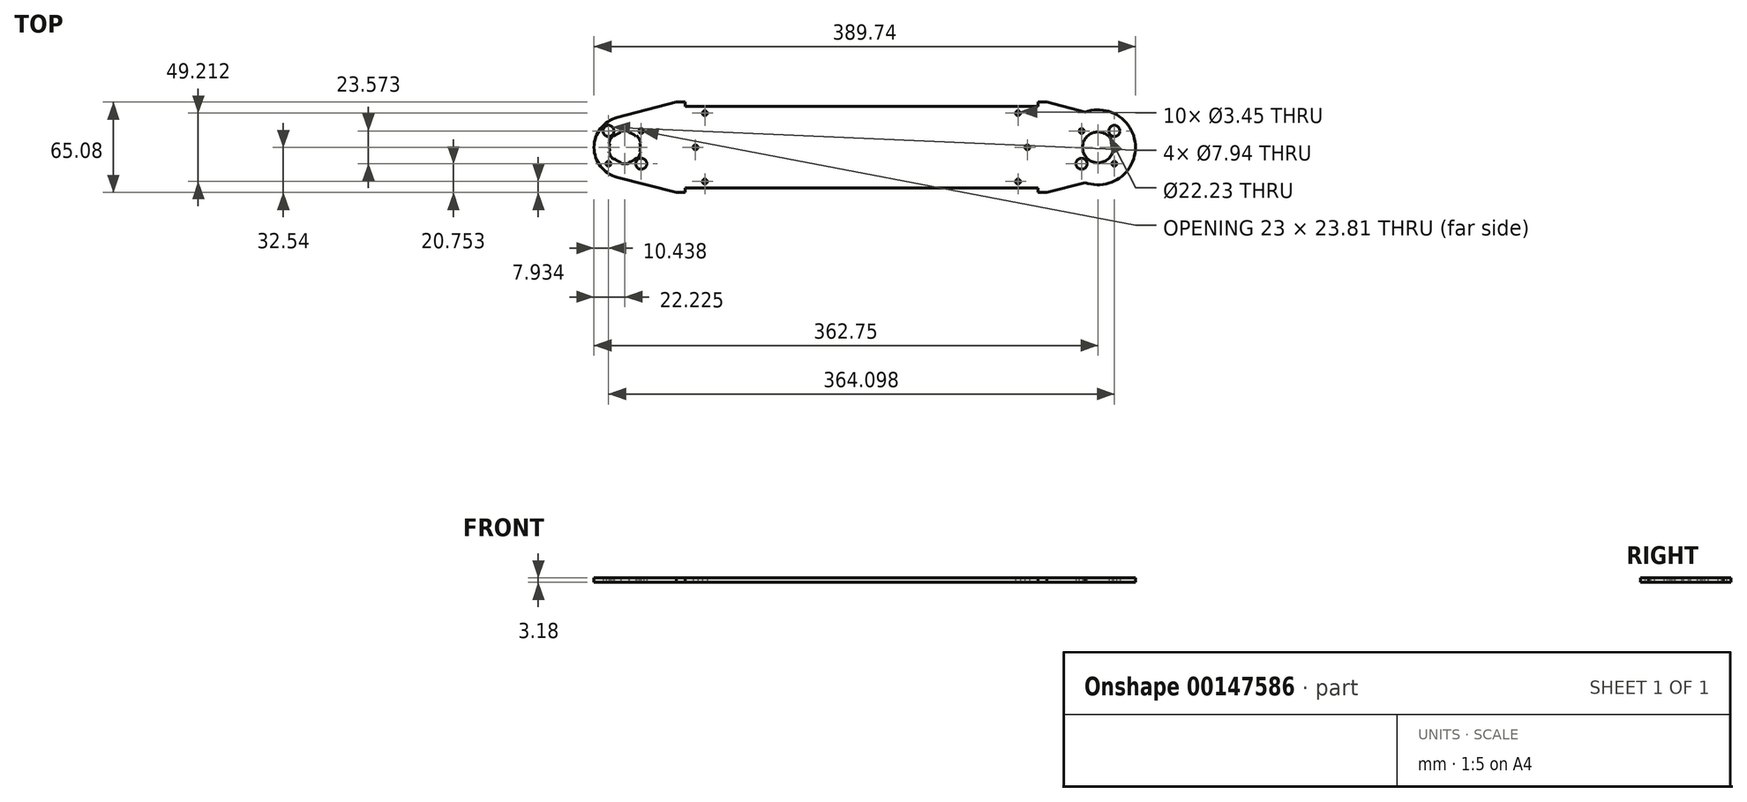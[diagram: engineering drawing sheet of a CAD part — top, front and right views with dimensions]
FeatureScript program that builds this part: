
annotation { "Feature Type Name" : "Feature", "Feature Type Description" : "" }
export const myFeature = defineFeature(function(context is Context, id is Id, definition is map)
    precondition{}
    {
        {
            var Q0;
            Q0=qCreatedBy(makeId("Top.planeOp"),FACE);
            var sketch = newSketch(context, id + "F0", { "sketchPlane" : qUnion([Q0])});
            skPoint(sketch, "E0.rect.middle", {"position": v(0, 0) * mm});
            skCircle(sketch, "E1", {"center": v(0, 0) * mm, "radius": 11.11 * mm});
            skLineSegment(sketch, "E2.bottom", {"start": v(11.79, 11.79) * mm, "end": v(-11.79, 11.79) * mm, "construction": true});
            skLineSegment(sketch, "E2.left", {"start": v(11.79, 11.79) * mm, "end": v(11.79, -11.79) * mm, "construction": true});
            skLineSegment(sketch, "E2.right", {"start": v(-11.79, 11.79) * mm, "end": v(-11.79, -11.79) * mm, "construction": true});
            skCircle(sketch, "E3", {"center": v(-11.79, 11.79) * mm, "radius": 1.73 * mm});
            skCircle(sketch, "E4", {"center": v(11.79, 11.79) * mm, "radius": 3.97 * mm});
            skCircle(sketch, "E5", {"center": v(11.79, -11.79) * mm, "radius": 1.73 * mm});
            skCircle(sketch, "E6", {"center": v(-11.79, -11.79) * mm, "radius": 3.97 * mm});
            skArc(sketch, "E7", {"start": v(-346.1, 21.51) * mm, "mid": v(-362.75, 0) * mm, "end": v(-346.1, -21.51) * mm});
            skLineSegment(sketch, "E8.bottom", {"start": v(-352.31, 11.79) * mm, "end": v(-328.74, 11.79) * mm, "construction": true});
            skLineSegment(sketch, "E8.top", {"start": v(-352.31, -11.79) * mm, "end": v(-328.74, -11.79) * mm, "construction": true});
            skLineSegment(sketch, "E8.left", {"start": v(-352.31, 11.79) * mm, "end": v(-352.31, -11.79) * mm, "construction": true});
            skLineSegment(sketch, "E8.right", {"start": v(-328.74, 11.79) * mm, "end": v(-328.74, -11.79) * mm, "construction": true});
            skCircle(sketch, "E9", {"center": v(-328.74, 11.79) * mm, "radius": 1.73 * mm});
            skCircle(sketch, "E10", {"center": v(-340.53, 0) * mm, "radius": 11.11 * mm});
            skCircle(sketch, "E11", {"center": v(-352.31, 11.79) * mm, "radius": 3.97 * mm});
            skCircle(sketch, "E12", {"center": v(-352.31, -11.79) * mm, "radius": 1.73 * mm});
            skCircle(sketch, "E13", {"center": v(-328.74, -11.79) * mm, "radius": 3.97 * mm});
            skLineSegment(sketch, "E14", {"start": v(0, 0) * mm, "end": v(-340.53, 0) * mm, "construction": true});
            skLineSegment(sketch, "E15", {"start": v(-346.1, -21.51) * mm, "end": v(-303.61, -32.54) * mm});
            skLineSegment(sketch, "E16", {"start": v(-346.1, 21.51) * mm, "end": v(-303.61, 32.54) * mm});
            skLineSegment(sketch, "E17", {"start": v(-297.26, -29.37) * mm, "end": v(-43.26, -29.37) * mm});
            skLineSegment(sketch, "E18", {"start": v(-297.26, 29.37) * mm, "end": v(-43.26, 29.37) * mm});
            skLineSegment(sketch, "E19", {"start": v(-297.26, 32.54) * mm, "end": v(-297.26, 29.37) * mm});
            skLineSegment(sketch, "E20", {"start": v(-297.26, 32.54) * mm, "end": v(-303.61, 32.54) * mm});
            skLineSegment(sketch, "E21", {"start": v(-297.26, -29.37) * mm, "end": v(-297.26, -32.54) * mm});
            skLineSegment(sketch, "E22", {"start": v(-297.26, -32.54) * mm, "end": v(-303.61, -32.54) * mm});
            skLineSegment(sketch, "E23", {"start": v(-43.26, -29.37) * mm, "end": v(-43.26, -32.54) * mm});
            skLineSegment(sketch, "E24", {"start": v(-43.26, -32.54) * mm, "end": v(-36.91, -32.54) * mm});
            skLineSegment(sketch, "E25", {"start": v(-43.26, 29.37) * mm, "end": v(-43.26, 32.54) * mm});
            skLineSegment(sketch, "E26", {"start": v(-43.26, 32.54) * mm, "end": v(-36.91, 32.54) * mm});
            skLineSegment(sketch, "E27", {"start": v(-36.91, -32.54) * mm, "end": v(-9.23, -25.36) * mm});
            skLineSegment(sketch, "E28", {"start": v(-9.23, 25.36) * mm, "end": v(-36.91, 32.54) * mm});
            skLineSegment(sketch, "E29", {"start": v(-297.26, 29.37) * mm, "end": v(-297.26, 24.6) * mm, "construction": true});
            skLineSegment(sketch, "E30", {"start": v(-297.26, 24.6) * mm, "end": v(-282.98, 24.6) * mm, "construction": true});
            skLineSegment(sketch, "E31", {"start": v(-297.26, -29.37) * mm, "end": v(-297.26, -24.6) * mm, "construction": true});
            skLineSegment(sketch, "E32", {"start": v(-297.26, -24.6) * mm, "end": v(-282.98, -24.6) * mm, "construction": true});
            skLineSegment(sketch, "E33", {"start": v(-43.26, -29.37) * mm, "end": v(-43.26, -24.6) * mm, "construction": true});
            skLineSegment(sketch, "E34", {"start": v(-43.26, -24.6) * mm, "end": v(-57.55, -24.6) * mm, "construction": true});
            skLineSegment(sketch, "E35", {"start": v(-43.26, 29.37) * mm, "end": v(-43.26, 24.6) * mm, "construction": true});
            skLineSegment(sketch, "E36", {"start": v(-43.26, 24.6) * mm, "end": v(-57.55, 24.6) * mm, "construction": true});
            skCircle(sketch, "E37", {"center": v(-282.98, 24.6) * mm, "radius": 1.73 * mm});
            skCircle(sketch, "E38", {"center": v(-57.55, 24.6) * mm, "radius": 1.73 * mm});
            skCircle(sketch, "E39", {"center": v(-57.55, -24.6) * mm, "radius": 1.73 * mm});
            skCircle(sketch, "E40", {"center": v(-282.98, -24.6) * mm, "radius": 1.73 * mm});
            skLineSegment(sketch, "E41", {"start": v(-11.79, -11.79) * mm, "end": v(11.79, -11.79) * mm, "construction": true});
            skLineSegment(sketch, "E42", {"start": v(-170.26, -29.37) * mm, "end": v(-170.26, 0) * mm, "construction": true});
            skLineSegment(sketch, "E43", {"start": v(-170.26, 0) * mm, "end": v(-170.26, 29.37) * mm, "construction": true});
            skArc(sketch, "E44", {"start": v(-9.23, -25.36) * mm, "mid": v(26.99, 0) * mm, "end": v(-9.23, 25.36) * mm});
            skLineSegment(sketch, "E45", {"start": v(-9.23, 25.36) * mm, "end": v(5.58, 21.51) * mm, "construction": true});
            skLineSegment(sketch, "E46", {"start": v(-9.23, -25.36) * mm, "end": v(5.58, -21.51) * mm, "construction": true});
            skArc(sketch, "E47", {"start": v(5.58, -21.51) * mm, "mid": v(22.23, 0) * mm, "end": v(5.58, 21.51) * mm, "construction": true});
            skLineSegment(sketch, "E48", {"start": v(-328.74, 11.79) * mm, "end": v(-289.73, 11.79) * mm, "construction": true});
            skLineSegment(sketch, "E49", {"start": v(-289.73, 11.79) * mm, "end": v(-289.73, 0) * mm, "construction": true});
            skLineSegment(sketch, "E50", {"start": v(-11.79, 11.79) * mm, "end": v(-50.8, 11.79) * mm, "construction": true});
            skLineSegment(sketch, "E51", {"start": v(-50.8, 11.79) * mm, "end": v(-50.8, 0) * mm, "construction": true});
            skCircle(sketch, "E52", {"center": v(-289.73, 0) * mm, "radius": 1.73 * mm});
            skCircle(sketch, "E53", {"center": v(-50.8, 0) * mm, "radius": 1.73 * mm});
            skCircle(sketch, "E54", {"center": v(11.79, 11.79) * mm, "radius": 5.56 * mm, "construction": true});
            skSolve(sketch);
        }
        {
            var Q0;
            Q0=qSketchRegion(id+"F0",true);
            extrude(context, id + "F1", {"entities" : qUnion([Q0]), "depth" : 3.17 * mm});
        }
        {
            var Q0;
            Q0=makeQuery(id+"F1.opExtrude","CAP_FACE",FACE,{"disambiguationData":[OSD([sQuery(id+"F0.wireOp",EDGE,"d63eafa0-1946-4b0e-8293-95e246b273c5.rect.bottom"),sQuery(id+"F0.wireOp",EDGE,"d63eafa0-1946-4b0e-8293-95e246b273c5.rect.top"),sQuery(id+"F0.wireOp",EDGE,"5983dcdd-59a7-4b72-80fd-e4567be1ae8a"),sQuery(id+"F0.wireOp",EDGE,"5a538b3e-fc2b-4d64-affd-5d60433388e5"),sQuery(id+"F0.wireOp",EDGE,"72e86de7-b207-474f-aadf-64543fae3f9b"),sQuery(id+"F0.wireOp",EDGE,"1c038800-5bd5-4753-8b38-6da13ef78ef9"),sQuery(id+"F0.wireOp",EDGE,"EbMUZoU6-Ffds-1dNq-SxhE-hPi8oSjhvaod"),sQuery(id+"F0.wireOp",EDGE,"RfgQjzcw-1Izs-lnTa-bWkk-oBHRDQjbZqQC"),sQuery(id+"F0.wireOp",EDGE,"1cCQAcjj-TyQA-3DMx-kDix-v5yZVaaGeXVM"),sQuery(id+"F0.wireOp",EDGE,"7KPu8lni-3ZWA-t6oJ-FRoh-C5MB3aVr7E9B"),sQuery(id+"F0.wireOp",EDGE,"bSzr06ES-7M0i-Fw5H-UJmt-4e4EQGRPIe4n"),sQuery(id+"F0.wireOp",EDGE,"WGsr6OjU-OX8l-mawA-7cCc-MfOuMOY06Cp5"),sQuery(id+"F0.wireOp",EDGE,"9mrz1cDN-18gM-20ra-6VCO-jp25g10tvNn2"),sQuery(id+"F0.wireOp",EDGE,"G0uOisy3-Mq6h-PcKh-Zkf4-CVoCvP3Hii1l"),sQuery(id+"F0.wireOp",EDGE,"1ae556be-0ab9-4322-b48e-98cf5a741ae0"),sQuery(id+"F0.wireOp",EDGE,"676cd913-43f8-42b3-8cdc-a90136d19ef5"),sQuery(id+"F0.wireOp",EDGE,"xnt2EyF8-ZVyQ-RbWD-GIsP-ThkcyX8ZioIH.bottom"),sQuery(id+"F0.wireOp",EDGE,"xnt2EyF8-ZVyQ-RbWD-GIsP-ThkcyX8ZioIH.top"),sQuery(id+"F0.wireOp",EDGE,"xnt2EyF8-ZVyQ-RbWD-GIsP-ThkcyX8ZioIH.left"),sQuery(id+"F0.wireOp",EDGE,"E1"),sQuery(id+"F0.wireOp",EDGE,"Jo9pZc7T-t0kF-vjz1-dNbX-L65bwNqtrrdz"),sQuery(id+"F0.wireOp",EDGE,"lEYoY9t7-PMOS-SVp6-xfnB-Xp9WdWMCDdum"),sQuery(id+"F0.wireOp",EDGE,"s7aM02SC-9XQ7-dueL-DqMg-ZFuJqOofj9mt"),sQuery(id+"F0.wireOp",EDGE,"deKa9ngt-XMq2-GGkr-SZIa-KlyN0U5bcCDe"),sQuery(id+"F0.wireOp",EDGE,"E3"),sQuery(id+"F0.wireOp",EDGE,"E4"),sQuery(id+"F0.wireOp",EDGE,"E5"),sQuery(id+"F0.wireOp",EDGE,"E6"),sQuery(id+"F0.wireOp",EDGE,"E7"),sQuery(id+"F0.wireOp",EDGE,"E9"),sQuery(id+"F0.wireOp",EDGE,"E10"),sQuery(id+"F0.wireOp",EDGE,"E11"),sQuery(id+"F0.wireOp",EDGE,"E12"),sQuery(id+"F0.wireOp",EDGE,"E13")])],"isStart":true});
            var sketch = newSketch(context, id + "F2", { "sketchPlane" : qUnion([Q0])});
            skLineSegment(sketch, "E55", {"start": v(-340.53, 0) * mm, "end": v(-350.15, -5.56) * mm, "construction": true});
            skArc(sketch, "E56", {"start": v(-351.26, -2.88) * mm, "mid": v(-350.15, -5.56) * mm, "end": v(-348.38, -7.86) * mm});
            skLineSegment(sketch, "E57", {"start": v(-340.53, 0) * mm, "end": v(-348.38, -7.86) * mm, "construction": true});
            skLineSegment(sketch, "E58", {"start": v(-340.53, 0) * mm, "end": v(-351.26, -2.88) * mm, "construction": true});
            skLineSegment(sketch, "E59", {"start": v(-348.38, -7.86) * mm, "end": v(-348.94, -8.42) * mm});
            skLineSegment(sketch, "E60", {"start": v(-351.26, -2.88) * mm, "end": v(-352.03, -3.08) * mm});
            skArc(sketch, "E61", {"start": v(-352.03, -3.08) * mm, "mid": v(-350.84, -5.95) * mm, "end": v(-348.94, -8.42) * mm});
            skLineSegment(sketch, "E62", {"start": v(-340.53, 0) * mm, "end": v(-351.64, 0) * mm, "construction": true});
            skSolve(sketch);
        }
        {
            var Q0;
            Q0=qSketchRegion(id+"F2",true);
            var Q1;
            Q1=makeQuery(id+"F1.opExtrude","CAP_FACE",FACE,{"disambiguationData":[OSD([sQuery(id+"F0.wireOp",EDGE,"d63eafa0-1946-4b0e-8293-95e246b273c5.rect.bottom"),sQuery(id+"F0.wireOp",EDGE,"d63eafa0-1946-4b0e-8293-95e246b273c5.rect.top"),sQuery(id+"F0.wireOp",EDGE,"5983dcdd-59a7-4b72-80fd-e4567be1ae8a"),sQuery(id+"F0.wireOp",EDGE,"5a538b3e-fc2b-4d64-affd-5d60433388e5"),sQuery(id+"F0.wireOp",EDGE,"72e86de7-b207-474f-aadf-64543fae3f9b"),sQuery(id+"F0.wireOp",EDGE,"1c038800-5bd5-4753-8b38-6da13ef78ef9"),sQuery(id+"F0.wireOp",EDGE,"EbMUZoU6-Ffds-1dNq-SxhE-hPi8oSjhvaod"),sQuery(id+"F0.wireOp",EDGE,"RfgQjzcw-1Izs-lnTa-bWkk-oBHRDQjbZqQC"),sQuery(id+"F0.wireOp",EDGE,"1cCQAcjj-TyQA-3DMx-kDix-v5yZVaaGeXVM"),sQuery(id+"F0.wireOp",EDGE,"7KPu8lni-3ZWA-t6oJ-FRoh-C5MB3aVr7E9B"),sQuery(id+"F0.wireOp",EDGE,"bSzr06ES-7M0i-Fw5H-UJmt-4e4EQGRPIe4n"),sQuery(id+"F0.wireOp",EDGE,"WGsr6OjU-OX8l-mawA-7cCc-MfOuMOY06Cp5"),sQuery(id+"F0.wireOp",EDGE,"9mrz1cDN-18gM-20ra-6VCO-jp25g10tvNn2"),sQuery(id+"F0.wireOp",EDGE,"G0uOisy3-Mq6h-PcKh-Zkf4-CVoCvP3Hii1l"),sQuery(id+"F0.wireOp",EDGE,"1ae556be-0ab9-4322-b48e-98cf5a741ae0"),sQuery(id+"F0.wireOp",EDGE,"676cd913-43f8-42b3-8cdc-a90136d19ef5"),sQuery(id+"F0.wireOp",EDGE,"xnt2EyF8-ZVyQ-RbWD-GIsP-ThkcyX8ZioIH.bottom"),sQuery(id+"F0.wireOp",EDGE,"xnt2EyF8-ZVyQ-RbWD-GIsP-ThkcyX8ZioIH.top"),sQuery(id+"F0.wireOp",EDGE,"xnt2EyF8-ZVyQ-RbWD-GIsP-ThkcyX8ZioIH.left"),sQuery(id+"F0.wireOp",EDGE,"E1"),sQuery(id+"F0.wireOp",EDGE,"Jo9pZc7T-t0kF-vjz1-dNbX-L65bwNqtrrdz"),sQuery(id+"F0.wireOp",EDGE,"lEYoY9t7-PMOS-SVp6-xfnB-Xp9WdWMCDdum"),sQuery(id+"F0.wireOp",EDGE,"s7aM02SC-9XQ7-dueL-DqMg-ZFuJqOofj9mt"),sQuery(id+"F0.wireOp",EDGE,"deKa9ngt-XMq2-GGkr-SZIa-KlyN0U5bcCDe"),sQuery(id+"F0.wireOp",EDGE,"E3"),sQuery(id+"F0.wireOp",EDGE,"E4"),sQuery(id+"F0.wireOp",EDGE,"E5"),sQuery(id+"F0.wireOp",EDGE,"E6"),sQuery(id+"F0.wireOp",EDGE,"E7"),sQuery(id+"F0.wireOp",EDGE,"E9"),sQuery(id+"F0.wireOp",EDGE,"E10"),sQuery(id+"F0.wireOp",EDGE,"E11"),sQuery(id+"F0.wireOp",EDGE,"E12"),sQuery(id+"F0.wireOp",EDGE,"E13")])],"isStart":false});
            extrude(context, id + "F3", {"entities" : qUnion([Q0]), "operationType" : NewBodyOperationType.REMOVE, "endBound" : BoundingType.UP_TO_SURFACE, "oppositeDirection" : true, "endBoundEntityFace" : qUnion([Q1]), "depth" : 25.4 * mm});
        }
        {
            var Q0;
            Q0=makeQuery(id+"F3.boolean.opBoolean","COPY",FACE,{"derivedFrom":makeQuery(id+"F3.opExtrude","SWEPT_FACE",FACE,{"disambiguationData":[OSD([sQuery(id+"F2.wireOp",EDGE,"E59")])]})});
            var Q1;
            Q1=makeQuery(id+"F3.boolean.opBoolean","COPY",FACE,{"derivedFrom":makeQuery(id+"F3.opExtrude","SWEPT_FACE",FACE,{"disambiguationData":[OSD([sQuery(id+"F2.wireOp",EDGE,"E61")])]})});
            var Q2;
            Q2=makeQuery(id+"F3.boolean.opBoolean","COPY",FACE,{"derivedFrom":makeQuery(id+"F3.opExtrude","SWEPT_FACE",FACE,{"disambiguationData":[OSD([sQuery(id+"F2.wireOp",EDGE,"E60")])]})});
            var Q3;
            Q3=makeQuery(id+"F1.opExtrude","SWEPT_FACE",FACE,{"disambiguationData":[OSD([sQuery(id+"F0.wireOp",EDGE,"E10")])]});
            circularPattern(context, id + "F4", {"patternType" : PatternType.FACE, "faces" : qUnion([Q0, Q1, Q2]), "axis" : qUnion([Q3]), "angle" : 60 * degree, "instanceCount" : 6});
        }
    });
